# Revit family: QF_BPRO_SAG L-3_574843
name_source: partatom
category: Sonderausstattung
revit_build: Autodesk Revit 2018 (Build: 20190510_1515(x64)
units: mm (PartAtom-declared; Revit-internal decimal feet)

## family parameters
Arbeitsebenenbasiert = Nein
Beim Laden mit Abzugskörper schneiden = Nein
Bemaßung runder Anschluss = Durchmesser verwenden
Gemeinsam genutzt = Nein
Immer vertikal = Ja
Raumberechnungspunkt = Ja
Teiletyp = Normal

## types (1)
- SAG L-3
    3fach = Ja
    Artikel Nummer = 574843
    Beckenlänge = 305 mm  [stored 1.00066 ft]
    Beckentiefe = 200 mm  [stored 0.656168 ft]
    Beschreibung = Speisenausgabewagen;
speziell für den Einsatz an einer Anfahrwand (Schiebegriff und Bedienelemente an der Längsseite);
3 Einzelbecken für 3x GN 1/1-200 oder deren Unterteilung;
mit Temperaturregler;
3 Schrankräume, beheizbar, mit je 6 Paar Auflagesicken für GN 1/1, Abstand: 57,5 mm
    Beschreibung durch Hersteller analog Leistungsverzeichniskurztext = Abmessungen (ohne Zubehör)

Länge:					1236 mm
Breite:					  746 mm
Höhe:					  933 mm


Ausführung

Aufbau
Der Speisenausgabewagen besteht komplett aus CNS 18/10. Die Oberfläche ist mikroliert. Die fugenlos eingeschweißten, tiefgezogenen Warmhaltebecken sind nass oder trocken getrennt voneinander beheiz- und regelbar. In die einzelnen Becken ist eine Markierung geprägt, welche der Füllmenge von 4 Litern entspricht. Um die Becken läuft ein Profilrand. Die Nummerierung der Becken ist in die Abdeckung geprägt. Jedes der Becken ist extra mit einem Ablasshahn und einem Ablaufrohr versehen (gemeinsamer Ablauf unterhalb des Bodens). Die Absperrung befindet sich in Griffhöhe an der Längsseite, bedienbar mittels Drehschalter.
Das Bedienfeld liegt vertieft mit Ein/Aus-Schalter, Kontrollleuchte, Spiralkabel, Blindsteckerbuchse und Temperaturregler an der Längsseite. Der Temperaturregler sichert die stufenlose Temperatureinstellung je Becken und Warmhaltefach.
Bedienseitig ist ein CNS-Sicherheits-Schiebegriff mit seitlichen Stoßschutzelementen aus Kunststoff (Polyamid) angebracht, welcher auch zum Schutz der Schalterelemente dient.
Fahrbar ist der Wagen mittels rostfreien Kunststoffrollen (2 Bockrollen und 2 Lenkrollen mit Feststeller mit 125 mm ø). Massive Stoßecken aus Kunststoff (Polyamid) an allen vier Ecken schützen vor Beschädigung.


Wagenkorpus
Der Wagenkorpus ist doppelwandig und isoliert.
Im Unterbau sind eingebaut:

•	drei beheizte, fugenlose Schrankfächer mit je 6 Paar tiefgezogenen Auflagesicken im Abstand von 57,5 mm, zur Aufnahme von GN-Behältern 
•	der Größe GN 1/1 oder deren Unterteilungen. Die Schrankraumhöhe beträgt 350 mm. Die Flügeltüren sind doppelwandig und isoliert und um 180° bzw. 270° schwenkbar. Die Schranktüren sind mit Griffmuscheln und einem selbsteinrastenden Verschluss versehen.


Zubehör/ Optionen

•	Klappbord an der Stirn- und/ oder den Längsseiten angebracht
•	Klappdeckel 1/3 zu 2/3, beide als Bord nutzbar
•	umlaufender Stoßschutz aus Kunststoff (Polyethylen)
•	Schiebedeckel mit Kugellagerführung
•	Hustenschutz aus ESG-Sicherheitsglas kundenseitig bis zur Abdeckung heruntergeführt oder kundenseitig mit einer Durchreichehöhe von 275 mm.
Optional mit Wärmebord aus CNS 
(mit 1 Keramikwärmestrahler je Bain-Marie, 250W, ungeregelt, separat zuschaltbar, 230V)
Länge Glasbord: 1040 mm
Höhe inkl. Aufsatz: ca. 1325 mm
•	GN-Deckel-Ablage, zur Aufnahme von GN-Deckel 1/1 und deren Unterteilung, stirnseitig angebracht
•	Zugdeichsel links oder rechts
•	weitere Rollenausführungen siehe Gesamt-Preisliste


Technische Daten

Werkstoff:		CNS 18/10
Gewicht:		85,5 kg 
Kapazität:		3 Warmhaltebecken
		3 beheizte Schrankfächer
Warmhaltebecken:	für GN 1/1-200 oder deren Unterteilung
		Temperatur von +30°C bis +95 °C regelbar 
Schrankfächer:		für je 6 x GN1/1 mit 6 Paar Auflagesicken (Abstand 57,5mm) 
Hygieneausführung H1
Temperatur von +30°C bis +85°C regelbar
Anschlusswert:		220-240V / 50Hz / 2,85 kW





Besonderheit

•	Strahlwassergeschützt (IPX 5)
•	um die Becken läuft ein Profilrand
•	die Becken sind nass oder trocken beheizbar
•	die Becken können einzeln beheizt und geregelt werden
•	die Schrankfächer können unabhängig von den Becken beheizt werden. 
•	geeignet für Optimierungsanlagen
•	Schrankfächer Hygieneausführung H1
•	gemäß DIN 18867, Teil 7


Fabrikat

Hersteller:			B.PRO
Modell:				SAG L-3
Best.Nr.				574 843
    Beschreibung durch Hersteller analog Leistungsverzeichnislangtext = Abmessungen (ohne Zubehör)

Länge:					1236 mm
Breite:					  746 mm
Höhe:					  933 mm


Ausführung

Aufbau
Der Speisenausgabewagen besteht komplett aus CNS 18/10. Die Oberfläche ist mikroliert. Die fugenlos eingeschweißten, tiefgezogenen Warmhaltebecken sind nass oder trocken getrennt voneinander beheiz- und regelbar. In die einzelnen Becken ist eine Markierung geprägt, welche der Füllmenge von 4 Litern entspricht. Um die Becken läuft ein Profilrand. Die Nummerierung der Becken ist in die Abdeckung geprägt. Jedes der Becken ist extra mit einem Ablasshahn und einem Ablaufrohr versehen (gemeinsamer Ablauf unterhalb des Bodens). Die Absperrung befindet sich in Griffhöhe an der Längsseite, bedienbar mittels Drehschalter.
Das Bedienfeld liegt vertieft mit Ein/Aus-Schalter, Kontrollleuchte, Spiralkabel, Blindsteckerbuchse und Temperaturregler an der Längsseite. Der Temperaturregler sichert die stufenlose Temperatureinstellung je Becken und Warmhaltefach.
Bedienseitig ist ein CNS-Sicherheits-Schiebegriff mit seitlichen Stoßschutzelementen aus Kunststoff (Polyamid) angebracht, welcher auch zum Schutz der Schalterelemente dient.
Fahrbar ist der Wagen mittels rostfreien Kunststoffrollen (2 Bockrollen und 2 Lenkrollen mit Feststeller mit 125 mm ø). Massive Stoßecken aus Kunststoff (Polyamid) an allen vier Ecken schützen vor Beschädigung.


Wagenkorpus
Der Wagenkorpus ist doppelwandig und isoliert.
Im Unterbau sind eingebaut:

•	drei beheizte, fugenlose Schrankfächer mit je 6 Paar tiefgezogenen Auflagesicken im Abstand von 57,5 mm, zur Aufnahme von GN-Behältern 
•	der Größe GN 1/1 oder deren Unterteilungen. Die Schrankraumhöhe beträgt 350 mm. Die Flügeltüren sind doppelwandig und isoliert und um 180° bzw. 270° schwenkbar. Die Schranktüren sind mit Griffmuscheln und einem selbsteinrastenden Verschluss versehen.


Zubehör/ Optionen

•	Klappbord an der Stirn- und/ oder den Längsseiten angebracht
•	Klappdeckel 1/3 zu 2/3, beide als Bord nutzbar
•	umlaufender Stoßschutz aus Kunststoff (Polyethylen)
•	Schiebedeckel mit Kugellagerführung
•	Hustenschutz aus ESG-Sicherheitsglas kundenseitig bis zur Abdeckung heruntergeführt oder kundenseitig mit einer Durchreichehöhe von 275 mm.
Optional mit Wärmebord aus CNS 
(mit 1 Keramikwärmestrahler je Bain-Marie, 250W, ungeregelt, separat zuschaltbar, 230V)
Länge Glasbord: 1040 mm
Höhe inkl. Aufsatz: ca. 1325 mm
•	GN-Deckel-Ablage, zur Aufnahme von GN-Deckel 1/1 und deren Unterteilung, stirnseitig angebracht
•	Zugdeichsel links oder rechts
•	weitere Rollenausführungen siehe Gesamt-Preisliste


Technische Daten

Werkstoff:		CNS 18/10
Gewicht:		85,5 kg 
Kapazität:		3 Warmhaltebecken
		3 beheizte Schrankfächer
Warmhaltebecken:	für GN 1/1-200 oder deren Unterteilung
		Temperatur von +30°C bis +95 °C regelbar 
Schrankfächer:		für je 6 x GN1/1 mit 6 Paar Auflagesicken (Abstand 57,5mm) 
Hygieneausführung H1
Temperatur von +30°C bis +85°C regelbar
Anschlusswert:		220-240V / 50Hz / 2,85 kW





Besonderheit

•	Strahlwassergeschützt (IPX 5)
•	um die Becken läuft ein Profilrand
•	die Becken sind nass oder trocken beheizbar
•	die Becken können einzeln beheizt und geregelt werden
•	die Schrankfächer können unabhängig von den Becken beheizt werden. 
•	geeignet für Optimierungsanlagen
•	Schrankfächer Hygieneausführung H1
•	gemäß DIN 18867, Teil 7


Fabrikat

Hersteller:			B.PRO
Modell:				SAG L-3
Best.Nr.				574 843
    Breite Korpus = 604 mm
    Elektrische leistung = 2850 W
    Frequenz = 50 Hz
    Gerätegewicht Netto = 85.50 kg
    Großküchengerätezuordnung = Ja
    Hauptschalter integriert = Ja
    Hersteller = B.PRO GmbH
    Höhe = 932 mm
    Höhe Arbeitsebene = 900 mm  [stored 2.95276 ft]
    Internetadresse Gerätehersteller = https://www.bpro-solutions.com
    Internetadresse für Ersatzteilliste = https://www.bpro-solutions.com
    Kosten = 5816 $
    Länge Gerätebreite = 1236 mm
    Länge Korpus = 1156 mm
    Material = QF_Metal-Stainless-Steel_general
    Material Dichtung = QF_Rubber-Black-Matt
    Material Kabel = QF_Rubber-Black-Matt
    Material Knöpfe1 = QF_Plastic-Black-Glossy
    Material Kunststoffteile = QF_Plastic-Black-Matt
    Material Metall glänzend = QF_Metal-Stainless-Steel_glossy
    Material Stoßschutz = QF_Rubber-Black-Matt
    Mittelabstand Schalter Strg = 92 mm  [stored 0.301837 ft]
    Modell = SAG L-3
    Schalldruckpegel = < 70 dB(A)
    Sockelhöhe = 160 mm  [stored 0.524934 ft]
    Spannung = 220 V
    Stecker System = Schuko Stecker
    Tiefe = 745 mm
    Typenkommentare = Speisenausgabewagen, 3 Becken, 3 Schränke
    Türbreite 2fach = 383 mm
    Türbreite Mitte = 380 mm
    URL = https://www.bpro-solutions.com
    Versatz Becken Mitte Strg = 0 mm  [stored 0 ft]
    Warnhinweise = Wenn das Gerät nicht für die vorliegende Netzspannung oder Netzfrequenz ausgelegt ist, kann die Geräteelektrik zerstört werden. Vor dem Anschließen sicherstellen, dass die auf dem Typenschild angegebene Netzspannung und Netzfrequenz mit den entsprechenden Werten der Netzsteckdose übereinstimmen.

Spannungsrisse durch kaltes Wasser in heißen Bain-Marie-Becken. Wenn in heiße Bain-Marie-Becken kaltes Wasser gefüllt wird, kann der rasche Temperaturwechsel Spannungsrisse verursachen, die zu Korrosion führen können. Vor dem Befüllen mit kaltem Wasser Bain-Marie-Becken abkühlen lassen oder heiße Bain-Marie-Becken mit heißem Wasser befüllen.

Eingeklemmter Fuß. Beim Lösen und Arretieren der Feststellbremse kann der Fuß eingeklemmt und dabei verletzt werden. Darauf achten, dass der Fuß nicht zwischen die Feststellbremse und die Stoßecke gerät.

Heiße Bain-Marie-Becken / Heiße Geräteflächn / Heiße Gastronormbehälter. Im Warmhaltebetrieb können Gerätebecken, Geräteflächen und darin enthaltene Gastronormbehälter oder andere Gegenstände heiß werden und Verbrennungen verursachen. Heiße Teile nur geschützt (z.B. mit Topflappen oder Schutzhandschuhe) anfassen.

Heiße flüssige Speisen. Heiße flüssige Speisen können über den Rand des Gastronormbehälters fließen und Verbrühungen verursachen. Gastronormbehälter waagerecht halten. Gastronormbehälter stets mit Dichtungsdeckeln verschließen.

Heißes Wasser. Bei Nassbeschickung befindet sich im Bain-Marie-Becken nach Gebrauch heißes Wasser. Wenn das heiße Wasser abgelassen wird, besteht die Gefahr von Verbrühungen. Gerät vor Reinigung abkühlen lassen.

Ausführliche Gefahrenhinweise entnehmen Sie der Betriebsanleitung.
    Zubehör = Nein
    Zuleitung zum Gerät im Lieferumfang = Ja

note: [stored X ft] marks values corroborated as IEEE doubles in the binary element streams (Revit-internal decimal feet)
